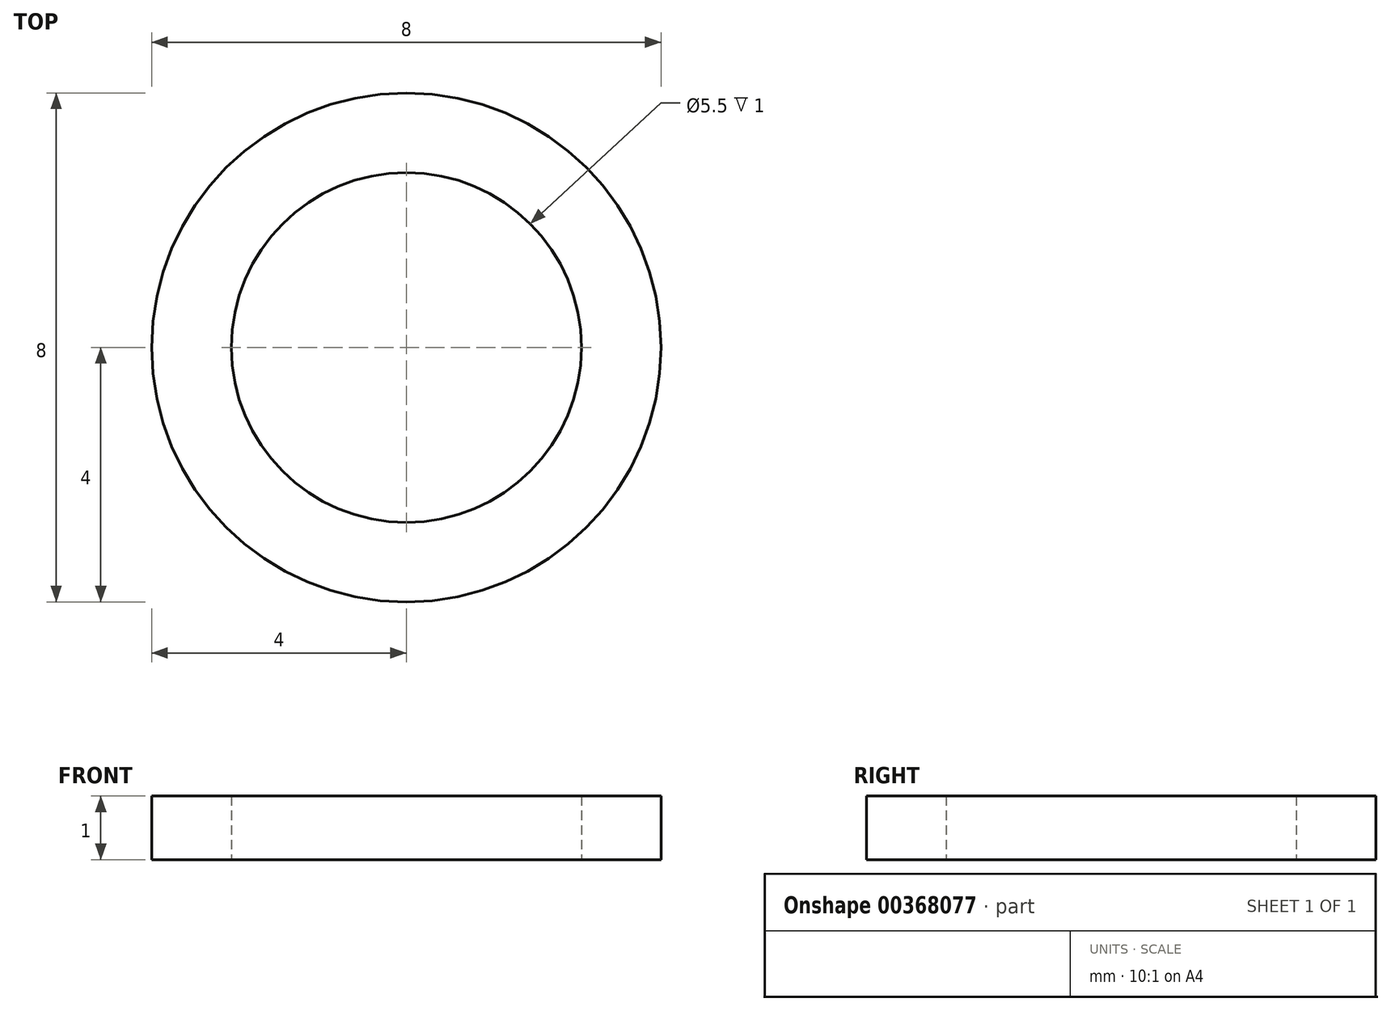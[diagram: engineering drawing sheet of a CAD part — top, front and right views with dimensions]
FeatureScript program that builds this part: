
annotation { "Feature Type Name" : "Feature", "Feature Type Description" : "" }
export const myFeature = defineFeature(function(context is Context, id is Id, definition is map)
    precondition{}
    {
        {
            var Q0;
            Q0=qCreatedBy(makeId("Top.planeOp"),FACE);
            var sketch = newSketch(context, id + "F0", { "sketchPlane" : qUnion([Q0])});
            skCircle(sketch, "E0", {"center": v(0, 0) * mm, "radius": 4 * mm});
            skCircle(sketch, "E1", {"center": v(0, 0) * mm, "radius": 2.75 * mm});
            skSolve(sketch);
        }
        {
            var Q0;
            Q0=makeQuery(id+"F0.imprint","IMPRINT",FACE,{"disambiguationData":[TD([[makeQuery(id+"F0.imprint","IMPRINT",EDGE,{"derivedFrom":sQuery(id+"F0.wireOp",EDGE,"E0")}),1.0]])]});
            extrude(context, id + "F1", {"entities" : qUnion([Q0]), "depth" : 1 * mm});
        }
    });
